# Revit family: VE_Exhaust Unit_MEPcontent_ClimaRad_MiniBox
name_source: partatom
category: Mechanical Equipment
revit_build: Autodesk Revit 2018 (Build: 20170223_1515(x64)
units: mm (PartAtom-declared; Revit-internal decimal feet)

## family parameters
Always vertical = No
Cut with Voids When Loaded = No
OmniClass Number = 23.75.70.21.31
OmniClass Title = Exhaust Terminals
Part Type = Normal
Room Calculation Point = Yes
Round Connector Dimension = Use Radius
Shared = No
Work Plane-Based = No

## types (1)
- MiniBox
    Article Description = Exhaust unit,includes: 4510408,4510407,4510405
    Article Type = MiniBox
    Base Family Version = 12.19
    Content Supplier URL = www.MEPcontent.com
    Custom = No
    Description = Exhaust unit,includes: 4510408,4510407,4510405
    EMCS Version = 4.0
    ETIM Article Class = EC001462
    Family Version = 10.04
    Height = 215 mm
    IFCExportAs = IfcAirTerminalBox
    IFCExportType = NOTDEFINED
    Length = 280 mm
    MEPcontent Class = EXHAUST_UNIT
    Manufacturer = ClimaRad
    Manufacturer Art. No. = 4510400
    Manufacturer URL = www.climarad.com
    Max Flow = 34.7 L/s
    Model = MiniBox
    Power = 25 W
    Product Line = ClimaRad
    Revit Version = 2018
    URL = https://mep.trimble.com
    Voltage = 230 V
    White = Color RAL 9003
    Width = 192 mm

## geometry (parser evidence)
native form markers: Sweep x8
no freeform markers — native parametric forms only
